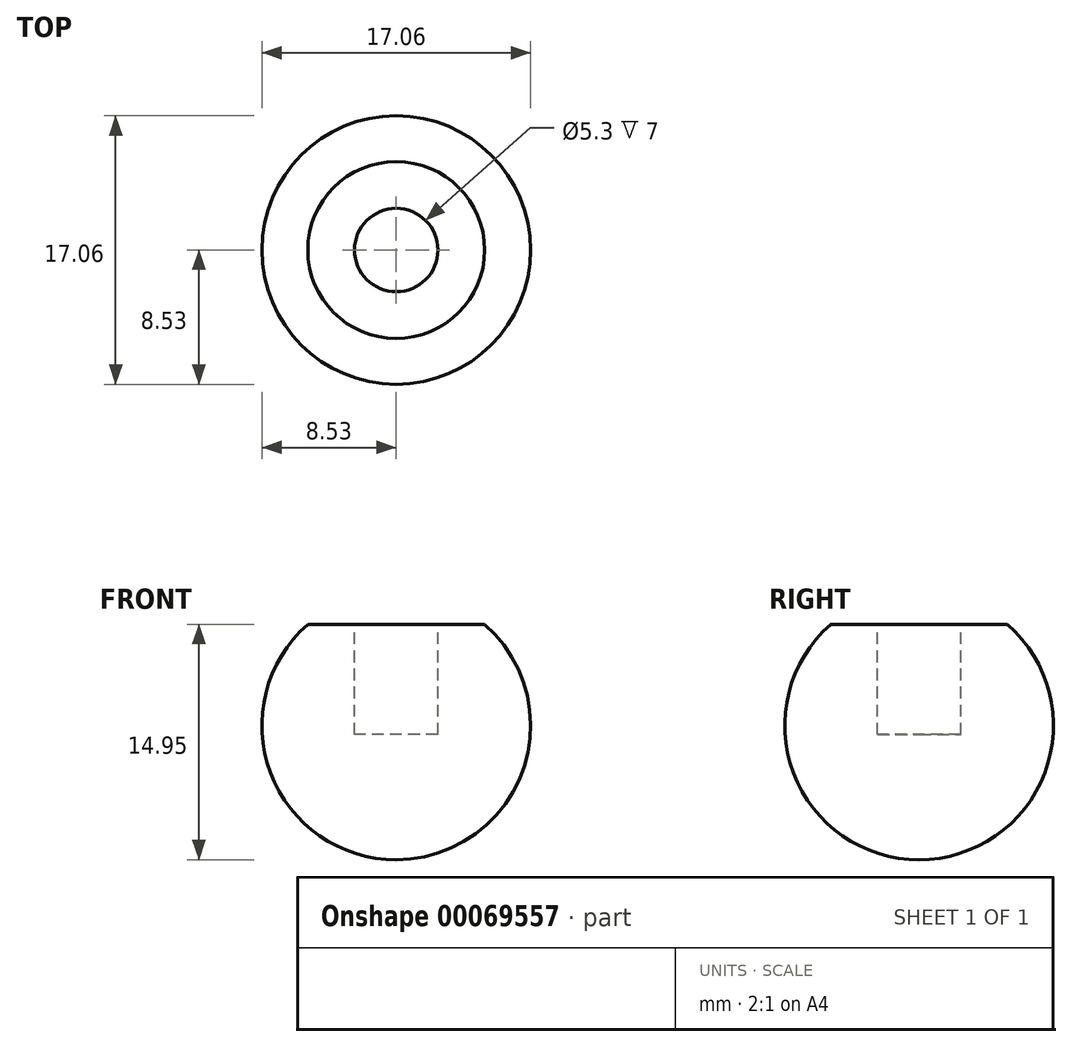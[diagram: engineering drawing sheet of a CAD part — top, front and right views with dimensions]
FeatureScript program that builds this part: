
annotation { "Feature Type Name" : "Feature", "Feature Type Description" : "" }
export const myFeature = defineFeature(function(context is Context, id is Id, definition is map)
    precondition{}
    {
        {
            var Q0;
            Q0=qCreatedBy(makeId("Front.planeOp"),FACE);
            var sketch = newSketch(context, id + "F0", { "sketchPlane" : qUnion([Q0])});
            skCircle(sketch, "E0", {"center": v(0, 0) * mm, "radius": 8.53 * mm});
            skLineSegment(sketch, "E1", {"start": v(0, 0) * mm, "end": v(0, 8.53) * mm});
            skLineSegment(sketch, "E2", {"start": v(0, 0) * mm, "end": v(0, -8.53) * mm});
            skSolve(sketch);
        }
        {
            var Q0;
            {var subQ0=sQuery(id+"F0.wireOp",EDGE,"E1");Q0=makeQuery(id+"F0.imprint","IMPRINT",FACE,{"disambiguationData":[TD([[makeQuery(id+"F0.imprint","IMPRINT",EDGE,{"derivedFrom":subQ0}),1.0]])]});}
            var Q1;
            Q1=sQuery(id+"F0.wireOp",EDGE,"E1");
            revolve(context, id + "F1", {"entities" : qUnion([Q0]), "axis" : qUnion([Q1]), "revolveType" : RevolveType.FULL});
        }
        {
            var Q0;
            Q0=qCreatedBy(makeId("Front.planeOp"),FACE);
            var sketch = newSketch(context, id + "F2", { "sketchPlane" : qUnion([Q0])});
            skLineSegment(sketch, "E3", {"start": v(0, 0) * mm, "end": v(0, 6.42) * mm});
            skLineSegment(sketch, "E4", {"start": v(0, 6.42) * mm, "end": v(-44.58, 6.42) * mm});
            skLineSegment(sketch, "E5", {"start": v(0, 6.42) * mm, "end": v(47.7, 6.42) * mm});
            skLineSegment(sketch, "E6", {"start": v(47.7, 6.42) * mm, "end": v(0, 28.33) * mm});
            skLineSegment(sketch, "E7", {"start": v(0, 28.33) * mm, "end": v(-44.58, 6.42) * mm});
            skLineSegment(sketch, "E8", {"start": v(0, 0) * mm, "end": v(0, -8.53) * mm});
            skLineSegment(sketch, "E9", {"start": v(0, -8.53) * mm, "end": v(0, 6.42) * mm});
            skSolve(sketch);
        }
        {
            var Q0;
            Q0=qSketchRegion(id+"F2",true);
            var Q1;
            Q1=makeQuery(id+"F2.imprint","IMPRINT",FACE,{"disambiguationData":[TD([[makeQuery(id+"F2.imprint","IMPRINT",EDGE,{"derivedFrom":sQuery(id+"F2.wireOp",EDGE,"E4")}),-1.0]])]});
            extrude(context, id + "F3", {"entities" : qUnion([Q0, Q1]), "operationType" : NewBodyOperationType.REMOVE, "endBound" : BoundingType.SYMMETRIC, "oppositeDirection" : true, "depth" : 40 * mm});
        }
        {
            var Q0;
            Q0=makeQuery(id+"F3.boolean.opBoolean","COPY",FACE,{"derivedFrom":makeQuery(id+"F3.opExtrude","SWEPT_FACE",FACE,{"disambiguationData":[OSD([sQuery(id+"F2.wireOp",EDGE,"E4"),sQuery(id+"F2.wireOp",EDGE,"E5")])]})});
            var sketch = newSketch(context, id + "F4", { "sketchPlane" : qUnion([Q0])});
            skCircle(sketch, "E10", {"center": v(0, 0) * mm, "radius": 2.65 * mm});
            skLineSegment(sketch, "E11", {"start": v(0, 0) * mm, "end": v(1.15, 2.39) * mm});
            skSolve(sketch);
        }
        {
            var Q0;
            Q0=makeQuery(id+"F4.imprint","IMPRINT",FACE,{"disambiguationData":[TD([[makeQuery(id+"F4.imprint","IMPRINT",EDGE,{"derivedFrom":sQuery(id+"F4.wireOp",EDGE,"E10")}),1.0]])]});
            extrude(context, id + "F5", {"entities" : qUnion([Q0]), "operationType" : NewBodyOperationType.REMOVE, "oppositeDirection" : true, "depth" : 7 * mm});
        }
    });
